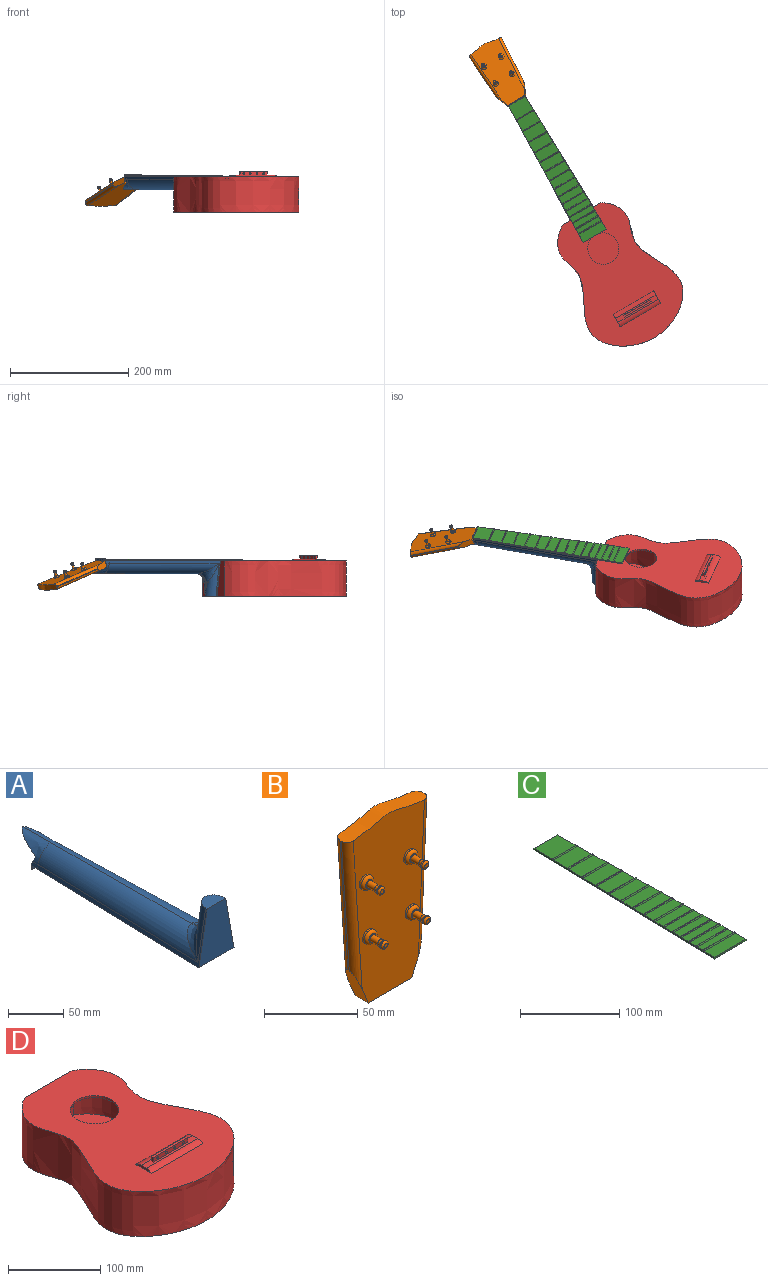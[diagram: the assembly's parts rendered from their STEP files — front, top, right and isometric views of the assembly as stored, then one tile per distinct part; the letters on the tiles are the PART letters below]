
ASSEMBLY  parts=4 mates=3
PART A: 51 faces, bbox 45.9x250x66.8 mm
  f0: plane 2.52x0.12mm, normal (0,0,-1), area 0.3mm2, adj f37,f39,f40,f41
  f1: plane 7.7x0.12mm, normal (0,0,-1), area 0.9mm2, adj f35,f38,f42,f45
  f2: plane 7x0.12mm, normal (0,0,-1), area 0.8mm2, adj f33,f36,f43,f46
  f3: plane 7x0.12mm, normal (0,0,-1), area 0.8mm2, adj f31,f34,f44,f47
  f4: plane 33x3.42mm, normal (0,-1,0), area 112.5mm2, adj f9,f27,f29,f31,f32,f33,f34,f35
  f5: plane 24.73x16.12mm, normal (0,0,1), area 283.7mm2, adj f6,f7,f8,f11,f12
  f6: plane 212.92x60mm, normal (-0.98,0.03,0.17), area 1078.5mm2, adj f5,f7,f9,f11,f13,f23
  f7: plane 60x45mm, normal (0,-1,0), area 2065mm2, adj f5,f6,f8,f9
  f8: plane 212.92x60mm, normal (0.98,0.03,0.17), area 1067.9mm2, adj f5,f7,f9,f12,f14,f21
  f9: plane 219.75x45mm, normal (0,0,-1), area 8529.1mm2, adj f4,f6,f7,f8,f21,f23
  f10: plane 10.53x3.7mm, normal (0.03,1,0), area 19.3mm2, adj f11,f12,f16,f17
  f11: cylinder r=13.64mm len=59.98mm, axis (-0.17,0,-0.98), area 828.4mm2, adj f5,f6,f10,f12,f18
  f12: cylinder r=13.64mm len=59.98mm, axis (-0.17,0,0.98), area 799.8mm2, adj f5,f8,f10,f11,f15
  f13: cylinder r=21.28mm len=211.61mm, axis (0.03,1,0), area 5210.4mm2, adj f6,f14,f17,f18,f22
  f14: cylinder r=21.28mm len=212.07mm, axis (0.03,-1,0), area 5216.5mm2, adj f8,f13,f15,f16,f17,f20
  f15: bspline ~34.32x29.75mm, area 300.1mm2, adj f12,f14,f16
  f16: bspline ~16.6x16.54mm, area 49.3mm2, adj f10,f14,f15,f17
  f17: torus R=37.58mm, axis (0.03,1,0), area 17.5mm2, adj f10,f13,f14,f16,f18
  f18: bspline ~34.17x29.37mm, area 302.9mm2, adj f11,f13,f17
  f19: plane 32.81x9.41mm, normal (0,0.94,0.34), area 306.9mm2, adj f20,f21,f22,f23,f24,f26
  f20: extruded ~36.16x16.93mm, area 468.9mm2, adj f14,f19,f21,f22,f24,f25
  f21: plane 8.47x4.46mm, normal (0.98,0,0.17), area 35mm2, adj f8,f9,f19,f20,f26,f29
  f22: extruded ~36.16x16.93mm, area 468.9mm2, adj f13,f19,f20,f23,f24,f25
  f23: plane 8.47x4.46mm, normal (-0.98,0,0.17), area 35mm2, adj f6,f9,f19,f22,f26,f27
  f24: plane 27.78x0.14mm, normal (0,0,-1), area 3.9mm2, adj f19,f20,f22,f25
  f25: plane 31.04x27.78mm, normal (0,0.34,-0.94), area 598mm2, adj f20,f22,f24
  f26: cylinder r=0.5mm len=33mm, axis (-1,0,0), area 31.8mm2, adj f19,f21,f23,f28
  f27: plane 3.42x1.09mm, normal (-1,0,0), area 3.7mm2, adj f4,f23,f28,f49
  f28: plane 33x3.42mm, normal (0,1,0), area 112.5mm2, adj f26,f27,f29,f31,f32,f33,f34,f35
  f29: plane 3.42x1.09mm, normal (1,0,0), area 3.7mm2, adj f4,f21,f28,f40
  f30: plane 2.52x0.12mm, normal (0,0,-1), area 0.3mm2, adj f32,f48,f49,f50
  f31: cylinder r=0.97mm len=1.09mm, axis (0,-1,0), area 0.9mm2, adj f3,f4,f28,f32,f44,f47
  f32: cylinder r=0.97mm len=1.09mm, axis (0,-1,0), area 0.9mm2, adj f4,f28,f30,f31,f48,f50
  f33: cylinder r=0.97mm len=1.09mm, axis (0,-1,0), area 0.9mm2, adj f2,f4,f28,f34,f43,f46
  f34: cylinder r=0.97mm len=1.09mm, axis (0,-1,0), area 0.9mm2, adj f3,f4,f28,f33,f44,f47
  f35: cylinder r=0.97mm len=1.09mm, axis (0,-1,0), area 0.9mm2, adj f1,f4,f28,f36,f42,f45
  f36: cylinder r=0.97mm len=1.09mm, axis (0,-1,0), area 0.9mm2, adj f2,f4,f28,f35,f43,f46
  f37: cylinder r=0.97mm len=1.09mm, axis (0,-1,0), area 1mm2, adj f0,f4,f28,f38,f39,f41
  f38: cylinder r=0.97mm len=1.09mm, axis (0,-1,0), area 1mm2, adj f1,f4,f28,f37,f42,f45
  f39: cylinder r=0.48mm len=3.32mm, axis (-1,0,0), area 2.2mm2, adj f0,f28,f37,f40
  f40: cylinder r=0.48mm len=1.09mm, axis (0,1,0), area 0.6mm2, adj f0,f29,f39,f41
  f41: cylinder r=0.48mm len=3.32mm, axis (1,0,0), area 2.2mm2, adj f0,f4,f37,f40
  f42: cylinder r=0.48mm len=8.34mm, axis (1,0,0), area 6.1mm2, adj f1,f4,f35,f38
  f43: cylinder r=0.48mm len=7.64mm, axis (1,0,0), area 5.6mm2, adj f2,f4,f33,f36
  f44: cylinder r=0.48mm len=7.64mm, axis (1,0,0), area 5.6mm2, adj f3,f4,f31,f34
  f45: cylinder r=0.48mm len=8.34mm, axis (-1,0,0), area 6.1mm2, adj f1,f28,f35,f38
  f46: cylinder r=0.48mm len=7.64mm, axis (-1,0,0), area 5.6mm2, adj f2,f28,f33,f36
  f47: cylinder r=0.48mm len=7.64mm, axis (-1,0,0), area 5.6mm2, adj f3,f28,f31,f34
  f48: cylinder r=0.48mm len=3.32mm, axis (1,0,0), area 2.2mm2, adj f4,f30,f32,f49
  f49: cylinder r=0.48mm len=1.09mm, axis (0,-1,0), area 0.6mm2, adj f27,f30,f48,f50
  f50: cylinder r=0.48mm len=3.32mm, axis (-1,0,0), area 2.2mm2, adj f28,f30,f32,f49
PART B: 44 faces, bbox 63x23x118.1 mm
  f0: plane 24x10mm, normal (0.92,0,-0.38), area 235mm2, adj f1,f5,f6,f7,f37,f39
  f1: plane 88x4mm, normal (1,0,-0.05), area 94mm2, adj f0,f2,f37,f39
  f2: extruded ~63x10mm, area 622.1mm2, adj f1,f3,f6,f7,f36,f37,f38,f39
  f3: plane 88x6mm, normal (-1,0,-0.07), area 94.2mm2, adj f2,f4,f36,f38
  f4: plane 24x10mm, normal (-0.92,0,-0.38), area 233.3mm2, adj f3,f5,f6,f7,f36,f38
  f5: plane 33x10mm, normal (0,0,-1), area 330mm2, adj f0,f4,f6,f7
  f6: plane 118.07x56.22mm, normal (0,-1,0), area 5174.7mm2, adj f0,f2,f4,f5,f8,f10,f12,f14
  f7: plane 118.07x56.22mm, normal (0,1,0), area 5429.2mm2, adj f0,f2,f4,f5,f36,f37
  f8: cylinder r=4.5mm len=9mm, axis (0,1,0), area 33.6mm2, adj f6,f19
  f9: plane 5.38x5.38mm, normal (0,-1,0), area 10.2mm2, adj f19,f20
  f10: cylinder r=4.5mm len=9mm, axis (0,1,0), area 33.6mm2, adj f6,f18
  f11: plane 5.38x5.38mm, normal (0,-1,0), area 10.2mm2, adj f18,f21
  f12: cylinder r=4.5mm len=9mm, axis (0,1,0), area 33.6mm2, adj f6,f17
  f13: plane 5.38x5.38mm, normal (0,-1,0), area 10.2mm2, adj f17,f23
  f14: cylinder r=4.5mm len=9mm, axis (0,1,0), area 33.6mm2, adj f6,f16
  f15: plane 5.38x5.38mm, normal (0,-1,0), area 10.2mm2, adj f16,f22
  f16: torus R=2.69mm, axis (0,-1,0), area 68.7mm2, adj f14,f15
  f17: torus R=2.69mm, axis (0,-1,0), area 68.7mm2, adj f12,f13
  f18: torus R=2.69mm, axis (0,-1,0), area 68.7mm2, adj f10,f11
  f19: torus R=2.69mm, axis (0,-1,0), area 68.7mm2, adj f8,f9
  f20: cylinder r=2mm len=5.95mm, axis (0,1,0), area 74.7mm2, adj f9,f35
  f21: cylinder r=2mm len=5.95mm, axis (0,1,0), area 74.7mm2, adj f11,f34
  f22: cylinder r=2mm len=5.95mm, axis (0,1,0), area 74.7mm2, adj f15,f32
  f23: cylinder r=2mm len=5.95mm, axis (0,1,0), area 74.7mm2, adj f13,f33
  f24: cylinder r=2.5mm len=5mm, axis (0,1,0), area 12.5mm2, adj f35,f42
  f25: plane 2.59x2.59mm, normal (0,-1,0), area 5.3mm2, adj f42
  f26: cylinder r=2.5mm len=5mm, axis (0,1,0), area 12.5mm2, adj f34,f41
  f27: plane 2.59x2.59mm, normal (0,-1,0), area 5.3mm2, adj f41
  f28: cylinder r=2.5mm len=5mm, axis (0,1,0), area 12.5mm2, adj f33,f40
  f29: plane 2.59x2.59mm, normal (0,-1,0), area 5.3mm2, adj f40
  f30: cylinder r=2.5mm len=5mm, axis (0,1,0), area 12.5mm2, adj f32,f43
  f31: plane 2.59x2.59mm, normal (0,-1,0), area 5.3mm2, adj f43
  f32: torus R=6.47mm, axis (0,-1,0), area 29.1mm2, adj f22,f30
  f33: torus R=6.47mm, axis (0,-1,0), area 29.1mm2, adj f23,f28
  f34: torus R=6.47mm, axis (0,-1,0), area 29.1mm2, adj f21,f26
  f35: torus R=6.47mm, axis (0,-1,0), area 29.1mm2, adj f20,f24
  f36: cylinder r=4.47mm len=101.45mm, axis (0.07,0,-1), area 652.4mm2, adj f2,f3,f4,f7
  f37: cylinder r=4.47mm len=100.56mm, axis (0.05,0,1), area 649.5mm2, adj f0,f1,f2,f7
  f38: cylinder r=4.47mm len=101.45mm, axis (-0.07,0,1), area 652.4mm2, adj f2,f3,f4,f6
  f39: cylinder r=4.47mm len=100.56mm, axis (-0.05,0,-1), area 649.5mm2, adj f0,f1,f2,f6
  f40: torus R=1.29mm, axis (0,-1,0), area 24.6mm2, adj f28,f29
  f41: torus R=1.29mm, axis (0,-1,0), area 24.6mm2, adj f26,f27
  f42: torus R=1.29mm, axis (0,-1,0), area 24.6mm2, adj f24,f25
  f43: torus R=1.29mm, axis (0,-1,0), area 24.6mm2, adj f30,f31
PART C: 82 faces, bbox 45x262.9x3 mm
  f0: plane 34.21x26.43mm, normal (0,0,1), area 888.2mm2, adj f15,f17,f18,f54
  f1: plane 35.21x22mm, normal (0,0,1), area 695.2mm2, adj f15,f17,f50,f51,f55,f56
  f2: plane 36.17x21mm, normal (0,0,1), area 679.1mm2, adj f15,f17,f48,f49,f57,f58
  f3: plane 37.08x20mm, normal (0,0,1), area 660.2mm2, adj f15,f17,f46,f47,f59,f60
  f4: plane 37.95x19mm, normal (0,0,1), area 638.6mm2, adj f15,f17,f44,f45,f61,f62
  f5: plane 38.77x18mm, normal (0,0,1), area 614.6mm2, adj f15,f17,f42,f43,f63,f64
  f6: plane 39.55x17mm, normal (0,0,1), area 588.1mm2, adj f15,f17,f40,f41,f65,f66
  f7: plane 40.28x16mm, normal (0,0,1), area 559.5mm2, adj f15,f17,f38,f39,f67,f68
  f8: plane 40.96x15mm, normal (0,0,1), area 528.7mm2, adj f15,f17,f36,f37,f69,f70
  f9: plane 41.6x14mm, normal (0,0,1), area 496mm2, adj f15,f17,f34,f35,f71,f72
  f10: plane 42.19x13mm, normal (0,0,1), area 461.5mm2, adj f15,f17,f32,f33,f73,f74
  f11: plane 42.74x12mm, normal (0,0,1), area 425.2mm2, adj f15,f17,f30,f31,f75,f76
  f12: plane 43.27x11.5mm, normal (0,0,1), area 409.1mm2, adj f15,f17,f28,f29,f77,f78
  f13: plane 43.77x11mm, normal (0,0,1), area 392.2mm2, adj f15,f17,f26,f27,f79,f80
  f14: plane 44.22x10mm, normal (0,0,1), area 352.4mm2, adj f15,f17,f24,f25,f52,f81
  f15: plane 262.93x6mm, normal (-1,0.02,0), area 526mm2, adj f0,f1,f2,f3,f4,f5,f6,f7
  f16: plane 45x2mm, normal (0,-1,0), area 90mm2, adj f15,f17,f19,f20
  f17: plane 262.93x6mm, normal (1,0.02,0), area 526mm2, adj f0,f1,f2,f3,f4,f5,f6,f7
  f18: plane 33x2mm, normal (0,1,0), area 66mm2, adj f0,f15,f17,f20
  f19: plane 45x17mm, normal (0,0,1), area 669.9mm2, adj f15,f16,f17,f22,f53
  f20: plane 262.93x45mm, normal (0,0,-1), area 10254.3mm2, adj f15,f16,f17,f18
  f21: plane 2x0.99mm, normal (1,0,0), area 1.4mm2, adj f23,f52,f53
  f22: plane 2x0.99mm, normal (-1,0,0), area 1.4mm2, adj f19,f52,f53
  f23: plane 2x0.05mm, normal (0,0,-1), area 0mm2, adj f17,f21,f52
  f24: plane 2x0.99mm, normal (-1,0,0), area 1.4mm2, adj f14,f80,f81
  f25: plane 2x0.99mm, normal (1,0,0), area 1.4mm2, adj f14,f80,f81
  f26: plane 2x0.99mm, normal (-1,0,0), area 1.4mm2, adj f13,f78,f79
  f27: plane 2x0.99mm, normal (1,0,0), area 1.4mm2, adj f13,f78,f79
  f28: plane 2x0.99mm, normal (-1,0,0), area 1.4mm2, adj f12,f76,f77
  f29: plane 2x0.99mm, normal (1,0,0), area 1.4mm2, adj f12,f76,f77
  f30: plane 2x0.99mm, normal (-1,0,0), area 1.4mm2, adj f11,f74,f75
  f31: plane 2x0.99mm, normal (1,0,0), area 1.4mm2, adj f11,f74,f75
  f32: plane 2x0.99mm, normal (-1,0,0), area 1.4mm2, adj f10,f72,f73
  f33: plane 2x0.99mm, normal (1,0,0), area 1.4mm2, adj f10,f72,f73
  f34: plane 2x0.99mm, normal (-1,0,0), area 1.4mm2, adj f9,f70,f71
  f35: plane 2x0.99mm, normal (1,0,0), area 1.4mm2, adj f9,f70,f71
  f36: plane 2x0.99mm, normal (-1,0,0), area 1.4mm2, adj f8,f68,f69
  f37: plane 2x0.99mm, normal (1,0,0), area 1.4mm2, adj f8,f68,f69
  f38: plane 2x0.99mm, normal (-1,0,0), area 1.4mm2, adj f7,f66,f67
  f39: plane 2x0.99mm, normal (1,0,0), area 1.4mm2, adj f7,f66,f67
  f40: plane 2x0.99mm, normal (-1,0,0), area 1.4mm2, adj f6,f64,f65
  f41: plane 2x0.99mm, normal (1,0,0), area 1.4mm2, adj f6,f64,f65
  f42: plane 2x0.99mm, normal (-1,0,0), area 1.4mm2, adj f5,f62,f63
  f43: plane 2x0.99mm, normal (1,0,0), area 1.4mm2, adj f5,f62,f63
  f44: plane 2x0.99mm, normal (-1,0,0), area 1.4mm2, adj f4,f60,f61
  f45: plane 2x0.99mm, normal (1,0,0), area 1.4mm2, adj f4,f60,f61
  f46: plane 2x0.99mm, normal (-1,0,0), area 1.4mm2, adj f3,f58,f59
  f47: plane 2x0.99mm, normal (1,0,0), area 1.4mm2, adj f3,f58,f59
  f48: plane 2x0.99mm, normal (-1,0,0), area 1.4mm2, adj f2,f56,f57
  f49: plane 2x0.99mm, normal (1,0,0), area 1.4mm2, adj f2,f56,f57
  f50: plane 2x0.99mm, normal (-1,0,0), area 1.4mm2, adj f1,f54,f55
  f51: plane 2x0.99mm, normal (1,0,0), area 1.4mm2, adj f1,f54,f55
  f52: cylinder r=1.21mm len=44.27mm, axis (1,0,0), area 66.3mm2, adj f14,f21,f22,f23,f53
  f53: cylinder r=1.21mm len=44.27mm, axis (1,0,0), area 66.3mm2, adj f19,f21,f22,f52
  f54: cylinder r=1.21mm len=34.21mm, axis (1,0,0), area 51.2mm2, adj f0,f50,f51,f55
  f55: cylinder r=1.21mm len=34.21mm, axis (1,0,0), area 51.2mm2, adj f1,f50,f51,f54
  f56: cylinder r=1.21mm len=35.21mm, axis (1,0,0), area 52.7mm2, adj f1,f48,f49,f57
  f57: cylinder r=1.21mm len=35.21mm, axis (1,0,0), area 52.7mm2, adj f2,f48,f49,f56
  f58: cylinder r=1.21mm len=36.17mm, axis (1,0,0), area 54.2mm2, adj f2,f46,f47,f59
  f59: cylinder r=1.21mm len=36.17mm, axis (1,0,0), area 54.2mm2, adj f3,f46,f47,f58
  f60: cylinder r=1.21mm len=37.08mm, axis (1,0,0), area 55.5mm2, adj f3,f44,f45,f61
  f61: cylinder r=1.21mm len=37.08mm, axis (1,0,0), area 55.5mm2, adj f4,f44,f45,f60
  f62: cylinder r=1.21mm len=37.95mm, axis (1,0,0), area 56.8mm2, adj f4,f42,f43,f63
  f63: cylinder r=1.21mm len=37.95mm, axis (1,0,0), area 56.8mm2, adj f5,f42,f43,f62
  f64: cylinder r=1.21mm len=38.77mm, axis (1,0,0), area 58.1mm2, adj f5,f40,f41,f65
  f65: cylinder r=1.21mm len=38.77mm, axis (1,0,0), area 58.1mm2, adj f6,f40,f41,f64
  f66: cylinder r=1.21mm len=39.55mm, axis (1,0,0), area 59.2mm2, adj f6,f38,f39,f67
  f67: cylinder r=1.21mm len=39.55mm, axis (1,0,0), area 59.2mm2, adj f7,f38,f39,f66
  f68: cylinder r=1.21mm len=40.28mm, axis (1,0,0), area 60.3mm2, adj f7,f36,f37,f69
  f69: cylinder r=1.21mm len=40.28mm, axis (1,0,0), area 60.3mm2, adj f8,f36,f37,f68
  f70: cylinder r=1.21mm len=40.96mm, axis (1,0,0), area 61.4mm2, adj f8,f34,f35,f71
  f71: cylinder r=1.21mm len=40.96mm, axis (1,0,0), area 61.4mm2, adj f9,f34,f35,f70
  f72: cylinder r=1.21mm len=41.6mm, axis (1,0,0), area 62.3mm2, adj f9,f32,f33,f73
  f73: cylinder r=1.21mm len=41.6mm, axis (1,0,0), area 62.3mm2, adj f10,f32,f33,f72
  f74: cylinder r=1.21mm len=42.19mm, axis (1,0,0), area 63.2mm2, adj f10,f30,f31,f75
  f75: cylinder r=1.21mm len=42.19mm, axis (1,0,0), area 63.2mm2, adj f11,f30,f31,f74
  f76: cylinder r=1.21mm len=42.74mm, axis (1,0,0), area 64mm2, adj f11,f28,f29,f77
  f77: cylinder r=1.21mm len=42.74mm, axis (1,0,0), area 64mm2, adj f12,f28,f29,f76
  f78: cylinder r=1.21mm len=43.27mm, axis (1,0,0), area 64.8mm2, adj f12,f26,f27,f79
  f79: cylinder r=1.21mm len=43.27mm, axis (1,0,0), area 64.8mm2, adj f13,f26,f27,f78
  f80: cylinder r=1.21mm len=43.77mm, axis (1,0,0), area 65.6mm2, adj f13,f24,f25,f81
  f81: cylinder r=1.21mm len=43.77mm, axis (1,0,0), area 65.6mm2, adj f14,f24,f25,f80
PART D: 23 faces, bbox 183.3x251.3x69 mm
  f0: plane 71.68x55mm, normal (0,-1,0), area 3942.5mm2, adj f1,f2,f3
  f1: extruded ~238x170.48mm, area 34101.9mm2, adj f0,f2,f3
  f2: plane 238.01x170.52mm, normal (0,0,-1), area 28012.9mm2, adj f0,f1,f4
  f3: plane 238.01x170.52mm, normal (0,0,1), area 30219mm2, adj f0,f1
  f4: cylinder r=26.5mm len=53mm, axis (0,0,1), area 416.3mm2, adj f2,f7
  f5: plane 72.94x60mm, normal (0,1,0), area 4376.4mm2, adj f6,f7,f8
  f6: extruded ~243x175.48mm, area 38064.1mm2, adj f5,f7,f8
  f7: plane 251.3x183.3mm, normal (0,0,1), area 27874mm2, adj f4,f5,f6,f9,f10,f12,f13
  f8: plane 251.3x183.3mm, normal (0,0,-1), area 31976.2mm2, adj f5,f6
  f9: plane 24x3mm, normal (-1,0,0), area 57mm2, adj f7,f11,f12,f13
  f10: plane 24x3mm, normal (1,0,0), area 57mm2, adj f7,f11,f12,f13
  f11: plane 79x8.07mm, normal (0,0,1), area 474.8mm2, adj f9,f10,f12,f13,f14,f15,f16,f17
  f12: cylinder r=12.07mm len=79mm, axis (1,0,0), area 687.1mm2, adj f7,f9,f10,f11
  f13: cylinder r=12.07mm len=79mm, axis (1,0,0), area 687.1mm2, adj f7,f9,f10,f11
  f14: plane 53x6mm, normal (0,1,0), area 289.7mm2, adj f11,f15,f17,f18,f19,f20,f21,f22
  f15: plane 6x3.07mm, normal (-1,0,0), area 18.4mm2, adj f11,f14,f16,f18
  f16: plane 53x6mm, normal (0,-1,0), area 289.7mm2, adj f11,f15,f17,f18,f19,f20,f21,f22
  f17: plane 6x3.07mm, normal (1,0,0), area 18.4mm2, adj f11,f14,f16,f18
  f18: plane 53x3.07mm, normal (0,0,1), area 162.8mm2, adj f14,f15,f16,f17
  f19: cylinder r=1.5mm len=3.07mm, axis (0,-1,0), area 29mm2, adj f14,f16
  f20: cylinder r=1.5mm len=3.07mm, axis (0,-1,0), area 29mm2, adj f14,f16
  f21: cylinder r=1.5mm len=3.07mm, axis (0,-1,0), area 29mm2, adj f14,f16
  f22: cylinder r=1.5mm len=3.07mm, axis (0,-1,0), area 29mm2, adj f14,f16
PLACE A rot(axis=(0.26,-0.97,0),180deg) t=(-650.5,97.18,-45.35)mm
PLACE B rot(axis=(-0.95,-0.25,0.18),112.7deg) t=(-666.57,179.83,-71.9)mm
PLACE C rot(axis=(0,0,1),30deg) t=(-535.86,-47.45,-45.35)mm
PLACE D rot(axis=(0,0,1),30deg) t=(-472.46,-152.8,-105.35)mm
MATE fastened A.f9 <-> C.f20  axis (0,0,1) through (-643.8,142.39,-45.35)mm
MATE fastened A.f19 <-> B.f5  axis (-0.47,0.81,-0.34) through (-643.75,142.3,-50.59)mm
MATE fastened A.f7 <-> D.f5  axis (0.5,-0.87,0) through (-533.92,-47.92,-45.35)mm
